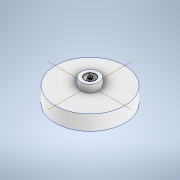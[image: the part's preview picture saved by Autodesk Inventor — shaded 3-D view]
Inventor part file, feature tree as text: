
AUTODESK INVENTOR PART (.ipt)
format: ipt  version: 2021.1 (Build 251245000, 245)  size: 127,488 bytes
history: native  units: in
note: dims shown in document units (in); Inventor stores cm internally (conversion verified against a paired STEP export)
features: extrude x4, sketch x4
ambient origin geometry x8: Origin, YZ Plane, XZ Plane, XY Plane, X Axis, Y Axis, Z Axis, Center Point
bodies: Solid1 (feature_tree)
feature tree (8):
  extrude  "Extrusion1"  Depth=2.4in
  extrude  "Extrusion2"  Depth=2.0in
  sketch  "Sketch3"  dims[d5=1.0in d6=0.0in d7=0.5in]
  sketch  "Sketch4"  dims[d8=1.4in d9=0.25in d10=0.0in d15=0.0in d16=0.0in d13=0.5in d14=0.0344in d17=0.5in d18=0.0344in]
  extrude  "Extrusion3"  Depth=1.0in
  extrude  "Extrusion6"  Depth=0.25in TaperAngle=0.0deg
  sketch  "Sketch1"  dims[d0=9.2in d1=2.4in]
  sketch  "Sketch2"  dims[d2=2.0in d3=0.0in d4=2.4in]
